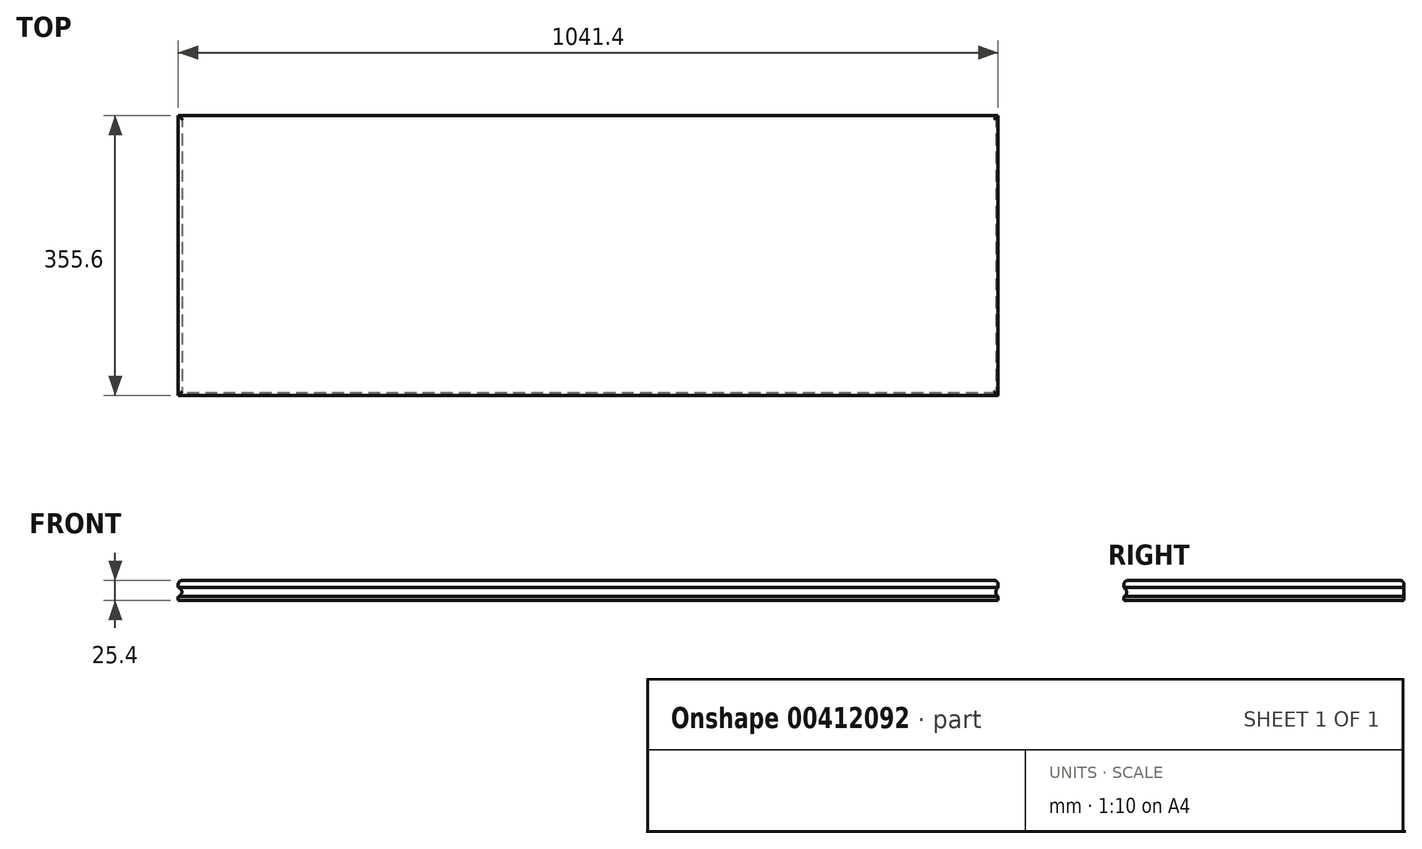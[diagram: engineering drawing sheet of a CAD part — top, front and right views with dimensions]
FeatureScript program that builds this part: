
annotation { "Feature Type Name" : "Feature", "Feature Type Description" : "" }
export const myFeature = defineFeature(function(context is Context, id is Id, definition is map)
    precondition{}
    {
        {
            var Q0;
            Q0=qCreatedBy(makeId("Top.planeOp"),FACE);
            var sketch = newSketch(context, id + "F0", { "sketchPlane" : qUnion([Q0])});
            skLineSegment(sketch, "E0.bottom", {"start": v(1041.4, 0) * mm, "end": v(0, 0) * mm});
            skLineSegment(sketch, "E0.top", {"start": v(1041.4, 355.6) * mm, "end": v(0, 355.6) * mm});
            skLineSegment(sketch, "E0.left", {"start": v(1041.4, 0) * mm, "end": v(1041.4, 355.6) * mm});
            skLineSegment(sketch, "E0.right", {"start": v(0, 0) * mm, "end": v(0, 355.6) * mm});
            skSolve(sketch);
        }
        {
            var Q0;
            Q0 = qSketchRegion(id + "F0", true);
            extrude(context, id + "F1", {"entities" : qUnion([Q0]), "oppositeDirection" : true, "depth" : 25.4 * mm});
        }
        {
            var Q0;
            Q0=makeQuery(id+"F1.opExtrude","CAP_FACE",FACE,{"disambiguationData":[OSD([sQuery(id+"F0.wireOp",EDGE,"E0.bottom"),sQuery(id+"F0.wireOp",EDGE,"E0.top"),sQuery(id+"F0.wireOp",EDGE,"E0.left"),sQuery(id+"F0.wireOp",EDGE,"E0.right")])],"isStart":true});
            fillet(context, id + "F2", {"entities" : qUnion([Q0]), "radius" : 5.08 * mm, "tangentPropagation" : true, "allowEdgeOverflow" : false});
        }
        {
            var Q0;
            Q0=makeQuery(id+"F1.opExtrude","SWEPT_FACE",FACE,{"disambiguationData":[OSD([sQuery(id+"F0.wireOp",EDGE,"E0.bottom")])]});
            var sketch = newSketch(context, id + "F3", { "sketchPlane" : qUnion([Q0])});
            skArc(sketch, "E1", {"start": v(0, -20.48) * mm, "mid": v(4.68, -14.78) * mm, "end": v(0, -9.08) * mm});
            skSolve(sketch);
        }
        {
            var Q0;
            {var subQ0=sQuery(id+"F3.wireOp",EDGE,"E1");Q0=makeQuery(id+"F3.imprint","IMPRINT",FACE,{"disambiguationData":[TD([[makeQuery(id+"F3.imprint","IMPRINT",EDGE,{"derivedFrom":subQ0}),1.0]])]});}
            extrude(context, id + "F4", {"entities" : qUnion([Q0]), "operationType" : NewBodyOperationType.REMOVE, "endBound" : BoundingType.THROUGH_ALL, "oppositeDirection" : true, "depth" : 25.4 * mm});
        }
        {
            var Q0;
            Q0=qCreatedBy(makeId("Right.planeOp"),FACE);
            var sketch = newSketch(context, id + "F5", { "sketchPlane" : qUnion([Q0])});
            skArc(sketch, "E2", {"start": v(0, -20.59) * mm, "mid": v(3.38, -14.9) * mm, "end": v(0, -9.2) * mm});
            skLineSegment(sketch, "E3", {"start": v(0, -20.59) * mm, "end": v(0, -9.2) * mm});
            skSolve(sketch);
        }
        {
            var Q0;
            Q0 = qSketchRegion(id + "F5", true);
            extrude(context, id + "F6", {"entities" : qUnion([Q0]), "operationType" : NewBodyOperationType.REMOVE, "endBound" : BoundingType.THROUGH_ALL, "depth" : 25.4 * mm});
        }
        {
            var Q0;
            {var subQ1=sQuery(id+"F0.wireOp",EDGE,"E0.bottom");Q0=makeQuery(id+"F6.boolean.opBoolean","SPLIT",FACE,{"disambiguationData":[TD([makeQuery(id+"F2.opFillet","BLEND_FACE",FACE,{"disambiguationData":[OSD([subQ1])]})])],"derivedFrom":makeQuery(id+"F1.opExtrude","SWEPT_FACE",FACE,{"disambiguationData":[OSD([subQ1])]})});}
            var sketch = newSketch(context, id + "F7", { "sketchPlane" : qUnion([Q0])});
            skArc(sketch, "E4", {"start": v(1041.4, -9.2) * mm, "mid": v(1038.53, -14.84) * mm, "end": v(1041.4, -20.48) * mm});
            skLineSegment(sketch, "E5", {"start": v(1041.4, -9.2) * mm, "end": v(1041.4, -20.48) * mm});
            skSolve(sketch);
        }
        {
            var Q0;
            Q0 = qSketchRegion(id + "F7", true);
            extrude(context, id + "F8", {"entities" : qUnion([Q0]), "operationType" : NewBodyOperationType.REMOVE, "endBound" : BoundingType.THROUGH_ALL, "oppositeDirection" : true, "depth" : 25.4 * mm});
        }
    });
